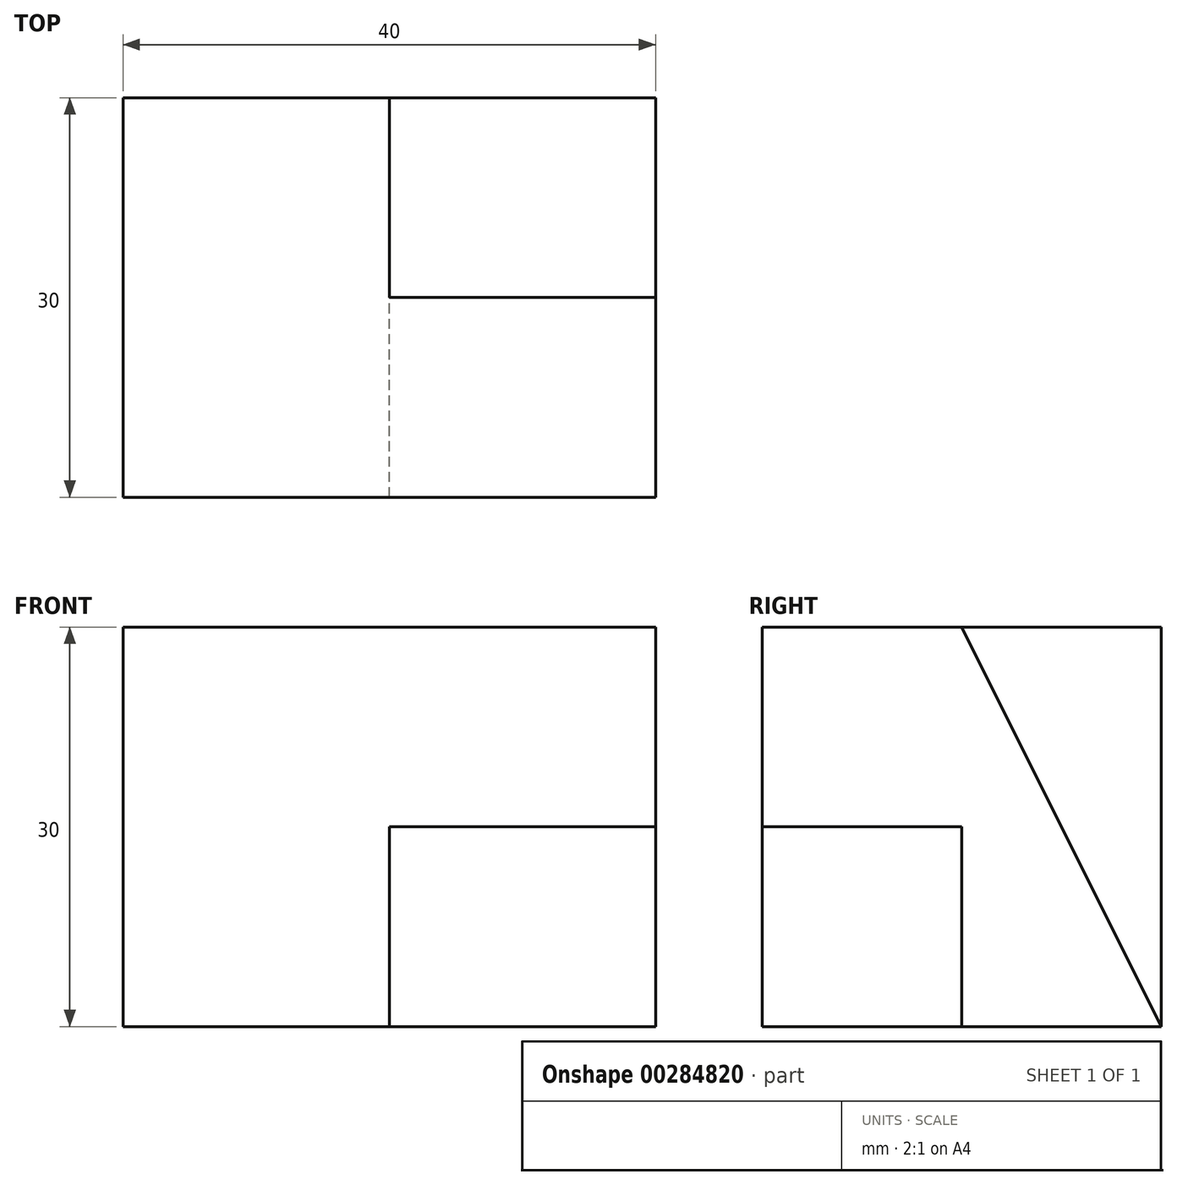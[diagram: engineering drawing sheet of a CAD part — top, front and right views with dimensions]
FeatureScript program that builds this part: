
annotation { "Feature Type Name" : "Feature", "Feature Type Description" : "" }
export const myFeature = defineFeature(function(context is Context, id is Id, definition is map)
    precondition{}
    {
        {
            var Q0;
            Q0=qCreatedBy(makeId("Right.planeOp"),FACE);
            var sketch = newSketch(context, id + "F0", { "sketchPlane" : qUnion([Q0])});
            skLineSegment(sketch, "E0.bottom", {"start": v(0, 0) * mm, "end": v(30, 0) * mm});
            skLineSegment(sketch, "E0.top", {"start": v(0, 30) * mm, "end": v(30, 30) * mm});
            skLineSegment(sketch, "E0.left", {"start": v(0, 0) * mm, "end": v(0, 30) * mm});
            skLineSegment(sketch, "E0.right", {"start": v(30, 0) * mm, "end": v(30, 30) * mm});
            skLineSegment(sketch, "E1", {"start": v(0, 15) * mm, "end": v(30, 15) * mm});
            skLineSegment(sketch, "E2", {"start": v(15, 30) * mm, "end": v(15, 0) * mm});
            skSolve(sketch);
        }
        {
            var Q0;
            Q0=qSketchRegion(id+"F0",true);
            extrude(context, id + "F1", {"entities" : qUnion([Q0]), "depth" : 20 * mm});
        }
        {
            var Q0;
            {var subQ0=sQuery(id+"F0.wireOp",EDGE,"E0.right");var subQ1=sQuery(id+"F0.wireOp",EDGE,"E0.bottom");var subQ2=makeQuery(id+"F0.imprint","INTERSECT",VERTEX,{"derivedFrom":[subQ1,subQ0]});Q0=makeQuery(id+"F0.imprint","IMPRINT",FACE,{"disambiguationData":[TD([[makeQuery(id+"F0.imprint","IMPRINT",EDGE,{"disambiguationData":[TD([[subQ2,1.0]])],"derivedFrom":subQ1}),1.0]])]});}
            var Q1;
            {var subQ0=sQuery(id+"F0.wireOp",EDGE,"E0.right");var subQ1=sQuery(id+"F0.wireOp",EDGE,"E0.top");var subQ2=makeQuery(id+"F0.imprint","INTERSECT",VERTEX,{"derivedFrom":[subQ1,subQ0]});Q1=makeQuery(id+"F0.imprint","IMPRINT",FACE,{"disambiguationData":[TD([[makeQuery(id+"F0.imprint","IMPRINT",EDGE,{"disambiguationData":[TD([[subQ2,1.0]])],"derivedFrom":subQ1}),-1.0]])]});}
            var Q2;
            {var subQ0=sQuery(id+"F0.wireOp",EDGE,"E0.left");var subQ1=sQuery(id+"F0.wireOp",EDGE,"E0.top");var subQ2=makeQuery(id+"F0.imprint","INTERSECT",VERTEX,{"derivedFrom":[subQ1,subQ0]});Q2=makeQuery(id+"F0.imprint","IMPRINT",FACE,{"disambiguationData":[TD([[makeQuery(id+"F0.imprint","IMPRINT",EDGE,{"disambiguationData":[TD([[subQ2,-1.0]])],"derivedFrom":subQ1}),-1.0]])]});}
            extrude(context, id + "F2", {"entities" : qUnion([Q0, Q1, Q2]), "operationType" : NewBodyOperationType.ADD, "depth" : 40 * mm});
        }
        {
            var Q0;
            Q0=makeQuery(id+"F2.opExtrude","CAP_FACE",FACE,{"disambiguationData":[OSD([sQuery(id+"F0.wireOp",EDGE,"E0.bottom"),sQuery(id+"F0.wireOp",EDGE,"E0.top"),sQuery(id+"F0.wireOp",EDGE,"E0.left"),sQuery(id+"F0.wireOp",EDGE,"E0.right"),sQuery(id+"F0.wireOp",EDGE,"E1"),sQuery(id+"F0.wireOp",EDGE,"E2")])],"isStart":false});
            var sketch = newSketch(context, id + "F3", { "sketchPlane" : qUnion([Q0])});
            skLineSegment(sketch, "E3", {"start": v(15, 30) * mm, "end": v(30, 0) * mm});
            skSolve(sketch);
        }
        {
            var Q0;
            Q0 = qSketchRegion(id + "F3", true);
            var Q1;
            {var subQ0=sQuery(id+"F3.wireOp",EDGE,"E3");Q1=makeQuery(id+"F3.imprint","IMPRINT",FACE,{"disambiguationData":[TD([[makeQuery(id+"F3.imprint","IMPRINT",EDGE,{"derivedFrom":subQ0}),1.0]])]});}
            extrude(context, id + "F4", {"entities" : qUnion([Q0, Q1]), "operationType" : NewBodyOperationType.REMOVE, "oppositeDirection" : true, "depth" : 20 * mm});
        }
    });
